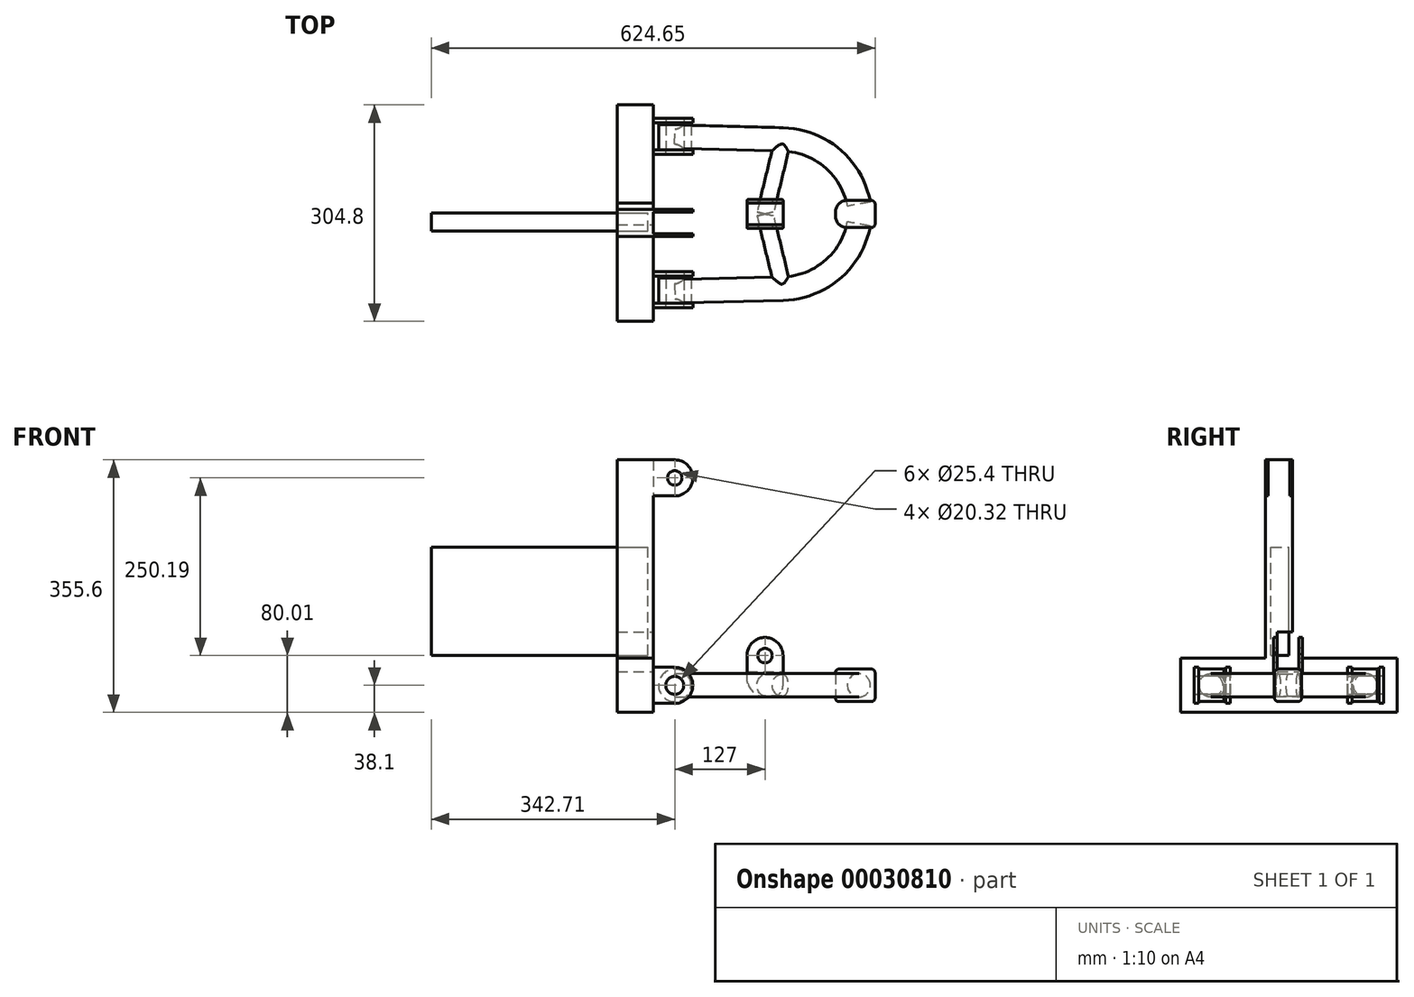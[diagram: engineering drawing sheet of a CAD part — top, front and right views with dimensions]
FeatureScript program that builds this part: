
annotation { "Feature Type Name" : "Feature", "Feature Type Description" : "" }
export const myFeature = defineFeature(function(context is Context, id is Id, definition is map)
    precondition{}
    {
        {
            var Q0;
            Q0=qCreatedBy(makeId("Front.planeOp"),FACE);
            var sketch = newSketch(context, id + "F0", { "sketchPlane" : qUnion([Q0])});
            skLineSegment(sketch, "E0.rect.bottom", {"start": v(-81.28, 38.1) * mm, "end": v(-30.48, 38.1) * mm});
            skLineSegment(sketch, "E0.rect.top", {"start": v(-81.28, -38.1) * mm, "end": v(-30.48, -38.1) * mm});
            skLineSegment(sketch, "E0.rect.left", {"start": v(-81.28, 38.1) * mm, "end": v(-81.28, -38.1) * mm});
            skLineSegment(sketch, "E0.rect.right", {"start": v(-30.48, 38.1) * mm, "end": v(-30.48, -38.1) * mm});
            skPoint(sketch, "E0.rect.middle", {"position": v(-55.88, 0) * mm});
            skCircle(sketch, "E1", {"center": v(0, 0) * mm, "radius": 12.7 * mm, "construction": true});
            skSolve(sketch);
        }
        {
            var Q0;
            Q0 = qSketchRegion(id + "F0", true);
            extrude(context, id + "F1", {"entities" : qUnion([Q0]), "endBound" : BoundingType.SYMMETRIC, "depth" : 304.8 * mm});
        }
        {
            var Q0;
            Q0=qCreatedBy(makeId("Front.planeOp"),FACE);
            cPlane(context, id + "F2", {"entities" : qUnion([Q0]), "cplaneType" : CPlaneType.OFFSET, "offset" : 127 * mm, "width" : 152.4 * mm, "height" : 152.4 * mm});
        }
        {
            var Q0;
            Q0=qCreatedBy(id+"F2.planeOp",FACE);
            cPlane(context, id + "F3", {"entities" : qUnion([Q0]), "cplaneType" : CPlaneType.OFFSET, "offset" : 38.1 * mm, "oppositeDirection" : true, "width" : 152.4 * mm, "height" : 152.4 * mm});
        }
        {
            var Q0;
            Q0=qCreatedBy(id+"F2.planeOp",FACE);
            var sketch = newSketch(context, id + "F4", { "sketchPlane" : qUnion([Q0])});
            skLineSegment(sketch, "E2.0", {"start": v(-30.48, 38.1) * mm, "end": v(-30.48, -38.1) * mm});
            skCircle(sketch, "E3", {"center": v(0, 0) * mm, "radius": 12.7 * mm});
            skLineSegment(sketch, "E4", {"start": v(-30.48, 25.4) * mm, "end": v(0, 25.4) * mm});
            skLineSegment(sketch, "E5", {"start": v(-30.48, -25.4) * mm, "end": v(0, -25.4) * mm});
            skArc(sketch, "E6", {"start": v(0, -25.4) * mm, "mid": v(25.4, 0) * mm, "end": v(0, 25.4) * mm});
            skLineSegment(sketch, "E7", {"start": v(0, 0) * mm, "end": v(-29.52, 0) * mm, "construction": true});
            skSolve(sketch);
        }
        {
            var Q0;
            Q0=qCreatedBy(id+"F3.planeOp",FACE);
            var sketch = newSketch(context, id + "F5", { "sketchPlane" : qUnion([Q0])});
            skLineSegment(sketch, "E8.0", {"start": v(-30.48, 25.4) * mm, "end": v(0, 25.4) * mm});
            skArc(sketch, "E8.1", {"start": v(0, -25.4) * mm, "mid": v(25.4, 0) * mm, "end": v(0, 25.4) * mm});
            skCircle(sketch, "E8.2", {"center": v(0, 0) * mm, "radius": 12.7 * mm});
            skLineSegment(sketch, "E8.3", {"start": v(-30.48, -25.4) * mm, "end": v(0, -25.4) * mm});
            skLineSegment(sketch, "E9.0", {"start": v(-30.48, 38.1) * mm, "end": v(-30.48, -38.1) * mm});
            skSolve(sketch);
        }
        {
            var Q0;
            Q0=makeQuery(id+"F4.imprint","IMPRINT",FACE,{"disambiguationData":[TD([[makeQuery(id+"F4.imprint","IMPRINT",EDGE,{"derivedFrom":sQuery(id+"F4.wireOp",EDGE,"E3")}),-1.0]])]});
            extrude(context, id + "F6", {"entities" : qUnion([Q0]), "depth" : 6.35 * mm});
        }
        {
            var Q0;
            {var subQ2=sQuery(id+"F5.wireOp",EDGE,"E8.0");Q0=makeQuery(id+"F5.imprint","IMPRINT",FACE,{"disambiguationData":[TD([[makeQuery(id+"F5.imprint","IMPRINT",EDGE,{"derivedFrom":subQ2}),-1.0]])]});}
            extrude(context, id + "F7", {"entities" : qUnion([Q0]), "oppositeDirection" : true, "depth" : 6.35 * mm});
        }
        {
            var Q0;
            Q0=makeQuery(id+"F7.opExtrude","SWEPT_BODY",BODY,{"disambiguationData":[OSD([sQuery(id+"F5.wireOp",EDGE,"E8.0"),sQuery(id+"F5.wireOp",EDGE,"E8.1"),sQuery(id+"F5.wireOp",EDGE,"E8.2"),sQuery(id+"F5.wireOp",EDGE,"E8.3"),sQuery(id+"F5.wireOp",EDGE,"E9.0")])]});
            var Q1;
            Q1=makeQuery(id+"F6.opExtrude","SWEPT_BODY",BODY,{"disambiguationData":[OSD([sQuery(id+"F4.wireOp",EDGE,"E2.0"),sQuery(id+"F4.wireOp",EDGE,"E3"),sQuery(id+"F4.wireOp",EDGE,"E4"),sQuery(id+"F4.wireOp",EDGE,"E5"),sQuery(id+"F4.wireOp",EDGE,"E6")])]});
            var Q2;
            Q2=qCreatedBy(makeId("Front.planeOp"),FACE);
            mirror(context, id + "F8", {"entities" : qUnion([Q0, Q1]), "mirrorPlane" : qUnion([Q2])});
        }
        {
            var Q0;
            Q0=makeQuery(id+"F8.opPattern","COPY",FACE,{"derivedFrom":makeQuery(id+"F7.opExtrude","CAP_FACE",FACE,{"disambiguationData":[OSD([sQuery(id+"F5.wireOp",EDGE,"E8.0"),sQuery(id+"F5.wireOp",EDGE,"E8.1"),sQuery(id+"F5.wireOp",EDGE,"E8.2"),sQuery(id+"F5.wireOp",EDGE,"E8.3"),sQuery(id+"F5.wireOp",EDGE,"E9.0")])],"isStart":true}),"instanceName":"1"});
            cPlane(context, id + "F9", {"entities" : qUnion([Q0]), "cplaneType" : CPlaneType.OFFSET, "offset" : 0 * mm, "width" : 152.4 * mm, "height" : 152.4 * mm});
        }
        {
            var Q0;
            Q0=qCreatedBy(id+"F2.planeOp",FACE);
            var sketch = newSketch(context, id + "F10", { "sketchPlane" : qUnion([Q0])});
            skCircle(sketch, "E10.0", {"center": v(0, 0) * mm, "radius": 12.7 * mm, "construction": true});
            skCircle(sketch, "E11", {"center": v(0, 0) * mm, "radius": 22.86 * mm});
            skSolve(sketch);
        }
        {
            var Q0;
            Q0 = qSketchRegion(id + "F10", true);
            extrude(context, id + "F11", {"entities" : qUnion([Q0]), "oppositeDirection" : true, "depth" : 35.56 * mm});
        }
        {
            var Q0;
            Q0=qCreatedBy(id+"F9.planeOp",FACE);
            var sketch = newSketch(context, id + "F12", { "sketchPlane" : qUnion([Q0])});
            skCircle(sketch, "E12.0", {"center": v(0, 0) * mm, "radius": 22.86 * mm});
            skSolve(sketch);
        }
        {
            var Q0;
            Q0=makeQuery(id+"F12.imprint","IMPRINT",FACE,{"disambiguationData":[TD([[makeQuery(id+"F12.imprint","IMPRINT",EDGE,{"derivedFrom":sQuery(id+"F12.wireOp",EDGE,"E12.0")}),1.0]])]});
            extrude(context, id + "F13", {"entities" : qUnion([Q0]), "depth" : 35.56 * mm});
        }
        {
            var Q0;
            Q0=makeQuery(id+"F1.opExtrude","SWEPT_FACE",FACE,{"disambiguationData":[OSD([sQuery(id+"F0.wireOp",EDGE,"E0.rect.bottom")])]});
            var sketch = newSketch(context, id + "F14", { "sketchPlane" : qUnion([Q0])});
            skLineSegment(sketch, "E13.0", {"start": v(-81.28, -152.4) * mm, "end": v(-81.28, 152.4) * mm});
            skLineSegment(sketch, "E13.1", {"start": v(-30.48, -152.4) * mm, "end": v(-30.48, 152.4) * mm});
            skLineSegment(sketch, "E14.bottom", {"start": v(-81.28, -33.02) * mm, "end": v(-30.48, -33.02) * mm});
            skLineSegment(sketch, "E14.top", {"start": v(-81.28, 5.08) * mm, "end": v(-30.48, 5.08) * mm});
            skLineSegment(sketch, "E14.left", {"start": v(-81.28, -33.02) * mm, "end": v(-81.28, 5.08) * mm});
            skLineSegment(sketch, "E14.right", {"start": v(-30.48, -33.02) * mm, "end": v(-30.48, 5.08) * mm});
            skSolve(sketch);
        }
        {
            var Q0;
            Q0 = qSketchRegion(id + "F14", true);
            extrude(context, id + "F15", {"entities" : qUnion([Q0]), "operationType" : NewBodyOperationType.ADD, "depth" : 279.4 * mm});
        }
        {
            var Q0;
            Q0=makeQuery(id+"F15.opExtrude","SWEPT_FACE",FACE,{"disambiguationData":[OSD([sQuery(id+"F14.wireOp",EDGE,"E14.bottom")])]});
            var sketch = newSketch(context, id + "F16", { "sketchPlane" : qUnion([Q0])});
            skPoint(sketch, "E15.0", {"position": v(-30.48, 317.5) * mm});
            skLineSegment(sketch, "E16.bottom", {"start": v(-30.48, 317.5) * mm, "end": v(0, 317.5) * mm});
            skLineSegment(sketch, "E16.top", {"start": v(-30.48, 266.7) * mm, "end": v(0, 266.7) * mm});
            skLineSegment(sketch, "E16.left", {"start": v(-30.48, 317.5) * mm, "end": v(-30.48, 266.7) * mm});
            skArc(sketch, "E17", {"start": v(0, 266.7) * mm, "mid": v(25.4, 292.1) * mm, "end": v(0, 317.5) * mm});
            skCircle(sketch, "E18", {"center": v(0, 292.1) * mm, "radius": 10.16 * mm});
            skSolve(sketch);
        }
        {
            var Q0;
            Q0=makeQuery(id+"F15.opExtrude","SWEPT_FACE",FACE,{"disambiguationData":[OSD([sQuery(id+"F14.wireOp",EDGE,"E14.top")])]});
            var sketch = newSketch(context, id + "F17", { "sketchPlane" : qUnion([Q0])});
            skLineSegment(sketch, "E19.0", {"start": v(30.48, 317.5) * mm, "end": v(30.48, 266.7) * mm});
            skLineSegment(sketch, "E19.1", {"start": v(30.48, 317.5) * mm, "end": v(0, 317.5) * mm});
            skLineSegment(sketch, "E19.2", {"start": v(30.48, 266.7) * mm, "end": v(0, 266.7) * mm});
            skArc(sketch, "E19.3", {"start": v(0, 266.7) * mm, "mid": v(-25.4, 292.1) * mm, "end": v(0, 317.5) * mm});
            skCircle(sketch, "E19.4", {"center": v(0, 292.1) * mm, "radius": 10.16 * mm});
            skSolve(sketch);
        }
        {
            var Q0;
            Q0=makeQuery(id+"F16.imprint","IMPRINT",FACE,{"disambiguationData":[TD([[makeQuery(id+"F16.imprint","IMPRINT",EDGE,{"derivedFrom":sQuery(id+"F16.wireOp",EDGE,"E16.bottom")}),-1.0]])]});
            extrude(context, id + "F18", {"entities" : qUnion([Q0]), "operationType" : NewBodyOperationType.ADD, "oppositeDirection" : true, "depth" : 3.8 * mm});
        }
        {
            var Q0;
            Q0=makeQuery(id+"F17.imprint","IMPRINT",FACE,{"disambiguationData":[TD([[makeQuery(id+"F17.imprint","IMPRINT",EDGE,{"derivedFrom":sQuery(id+"F17.wireOp",EDGE,"E19.0")}),-1.0]])]});
            extrude(context, id + "F19", {"entities" : qUnion([Q0]), "operationType" : NewBodyOperationType.ADD, "oppositeDirection" : true, "depth" : 3.8 * mm});
        }
        {
            var Q0;
            Q0=qCreatedBy(makeId("Top.planeOp"),FACE);
            var sketch = newSketch(context, id + "F20", { "sketchPlane" : qUnion([Q0])});
            skLineSegment(sketch, "E20.0", {"start": v(-22.86, 124.46) * mm, "end": v(22.86, 124.46) * mm});
            skPoint(sketch, "E20.1", {"position": v(0, 88.9) * mm});
            skLineSegment(sketch, "E20.2", {"start": v(22.86, -91.44) * mm, "end": v(-22.86, -91.44) * mm});
            skPoint(sketch, "E20.3", {"position": v(0, -127) * mm});
            skLineSegment(sketch, "E21", {"start": v(0, -91.44) * mm, "end": v(0, -127) * mm, "construction": true});
            skLineSegment(sketch, "E22", {"start": v(0, 88.9) * mm, "end": v(0, 124.46) * mm, "construction": true});
            skLineSegment(sketch, "E23.rect.bottom", {"start": v(281.94, 17.78) * mm, "end": v(226.06, 17.78) * mm});
            skLineSegment(sketch, "E23.rect.top", {"start": v(281.94, -20.32) * mm, "end": v(226.06, -20.32) * mm});
            skLineSegment(sketch, "E23.rect.left", {"start": v(281.94, 17.78) * mm, "end": v(281.94, -20.32) * mm});
            skLineSegment(sketch, "E23.rect.right", {"start": v(226.06, 17.78) * mm, "end": v(226.06, -20.32) * mm});
            skPoint(sketch, "E23.rect.middle", {"position": v(254, -1.27) * mm});
            skLineSegment(sketch, "E24.0", {"start": v(22.86, -85.1) * mm, "end": v(-22.86, -85.1) * mm});
            skLineSegment(sketch, "E25", {"start": v(0, 107.7) * mm, "end": v(152.4, 103.7) * mm});
            skLineSegment(sketch, "E26.0", {"start": v(22.86, -127) * mm, "end": v(-22.86, -127) * mm});
            skLineSegment(sketch, "E27", {"start": v(22.86, 124.46) * mm, "end": v(22.86, -127) * mm, "construction": true});
            skPoint(sketch, "E28", {"position": v(22.86, -1.27) * mm});
            skLineSegment(sketch, "E29", {"start": v(22.86, -1.27) * mm, "end": v(68.58, -1.27) * mm, "construction": true});
            skArc(sketch, "E30", {"start": v(152.4, 103.7) * mm, "mid": v(221.84, 77.07) * mm, "end": v(259.08, 12.7) * mm});
            skLineSegment(sketch, "E31.rect.bottom", {"start": v(151.13, 19.05) * mm, "end": v(102.87, 19.05) * mm});
            skLineSegment(sketch, "E31.rect.top", {"start": v(151.13, -21.59) * mm, "end": v(102.87, -21.59) * mm});
            skLineSegment(sketch, "E31.rect.left", {"start": v(152.4, 17.78) * mm, "end": v(152.4, -20.32) * mm});
            skLineSegment(sketch, "E31.rect.right", {"start": v(101.6, 17.78) * mm, "end": v(101.6, -20.32) * mm});
            skPoint(sketch, "E31.rect.middle", {"position": v(127, -1.27) * mm});
            skLineSegment(sketch, "E32", {"start": v(127, -1.27) * mm, "end": v(152.4, 103.7) * mm});
            skPoint(sketch, "E33.visualSharp", {"position": v(101.6, 19.05) * mm});
            skArc(sketch, "E33.filletArc", {"start": v(102.87, 19.05) * mm, "mid": v(101.97, 18.68) * mm, "end": v(101.6, 17.78) * mm});
            skPoint(sketch, "E34.visualSharp", {"position": v(152.4, 19.05) * mm});
            skArc(sketch, "E34.filletArc", {"start": v(152.4, 17.78) * mm, "mid": v(152.03, 18.68) * mm, "end": v(151.13, 19.05) * mm});
            skPoint(sketch, "E35.visualSharp", {"position": v(152.4, -21.59) * mm});
            skArc(sketch, "E35.filletArc", {"start": v(151.13, -21.59) * mm, "mid": v(152.03, -21.22) * mm, "end": v(152.4, -20.32) * mm});
            skPoint(sketch, "E36.visualSharp", {"position": v(101.6, -21.59) * mm});
            skArc(sketch, "E36.filletArc", {"start": v(101.6, -20.32) * mm, "mid": v(101.97, -21.22) * mm, "end": v(102.87, -21.59) * mm});
            skSolve(sketch);
        }
        {
            var Q0;
            Q0=makeQuery(id+"F20.imprint","IMPRINT",FACE,{"disambiguationData":[TD([[makeQuery(id+"F20.imprint","IMPRINT",EDGE,{"derivedFrom":sQuery(id+"F20.wireOp",EDGE,"E23.rect.bottom")}),-1.0]])]});
            var Q1;
            Q1=makeQuery(id+"F20.imprint","IMPRINT",FACE,{"disambiguationData":[TD([[makeQuery(id+"F20.imprint","IMPRINT",EDGE,{"derivedFrom":sQuery(id+"F20.wireOp",EDGE,"E23.rect.bottom")}),1.0]])]});
            extrude(context, id + "F21", {"entities" : qUnion([Q0, Q1]), "endBound" : BoundingType.SYMMETRIC, "depth" : 45.72 * mm});
        }
        {
            var Q0;
            Q0=sQuery(id+"F20.wireOp",EDGE,"E25");
            var Q1;
            Q1=sQuery(id+"F20.wireOp",VERTEX,"E25.start");
            cPlane(context, id + "F22", {"entities" : qUnion([Q0, Q1]), "cplaneType" : CPlaneType.LINE_POINT, "offset" : 152.4 * mm, "width" : 152.4 * mm, "height" : 152.4 * mm});
        }
        {
            var Q0;
            Q0=qCreatedBy(id+"F22.planeOp",FACE);
            var sketch = newSketch(context, id + "F23", { "sketchPlane" : qUnion([Q0])});
            skCircle(sketch, "E37", {"center": v(107.66, 0) * mm, "radius": 16.51 * mm});
            skSolve(sketch);
        }
        {
            var Q0;
            Q0=makeQuery(id+"F23.imprint","IMPRINT",FACE,{"disambiguationData":[TD([[makeQuery(id+"F23.imprint","IMPRINT",EDGE,{"derivedFrom":sQuery(id+"F23.wireOp",EDGE,"E37")}),1.0]])]});
            var Q1;
            Q1=sQuery(id+"F20.wireOp",EDGE,"E25");
            var Q2;
            Q2=sQuery(id+"F20.wireOp",EDGE,"E30");
            sweep(context, id + "F24", {"profiles" : qUnion([Q0]), "path" : qUnion([Q1, Q2])});
        }
        {
            var Q0;
            Q0=sQuery(id+"F20.wireOp",EDGE,"E32");
            var Q1;
            Q1=sQuery(id+"F20.wireOp",VERTEX,"E31.rect.middle");
            cPlane(context, id + "F25", {"entities" : qUnion([Q0, Q1]), "cplaneType" : CPlaneType.LINE_POINT, "offset" : 152.4 * mm, "width" : 152.4 * mm, "height" : 152.4 * mm});
        }
        {
            var Q0;
            Q0=qCreatedBy(id+"F25.planeOp",FACE);
            var sketch = newSketch(context, id + "F26", { "sketchPlane" : qUnion([Q0])});
            skEllipse(sketch, "E38", {"center": v(-123.74, 0) * mm, "majorRadius": 11.43 * mm, "minorRadius": 15.24 * mm, "majorAxis": v(-1, 0)});
            skLineSegment(sketch, "E39", {"start": v(-123.74, 0) * mm, "end": v(-139.12, 0) * mm, "construction": true});
            skLineSegment(sketch, "E40", {"start": v(-123.74, 15.24) * mm, "end": v(-123.74, 0) * mm, "construction": true});
            skSolve(sketch);
        }
        {
            var Q0;
            Q0=makeQuery(id+"F26.imprint","IMPRINT",FACE,{"disambiguationData":[TD([[makeQuery(id+"F26.imprint","IMPRINT",EDGE,{"derivedFrom":sQuery(id+"F26.wireOp",EDGE,"E38")}),1.0]])]});
            var Q1;
            Q1=sQuery(id+"F20.wireOp",EDGE,"E32");
            sweep(context, id + "F27", {"operationType" : NewBodyOperationType.ADD, "profiles" : qUnion([Q0]), "path" : qUnion([Q1])});
        }
        {
            var Q0;
            Q0=makeQuery(id+"F20.imprint","IMPRINT",FACE,{"disambiguationData":[TD([[makeQuery(id+"F20.imprint","IMPRINT",EDGE,{"derivedFrom":sQuery(id+"F20.wireOp",EDGE,"E31.rect.top")}),-1.0]])]});
            extrude(context, id + "F28", {"entities" : qUnion([Q0]), "oppositeDirection" : true, "depth" : 16.5 * mm, "hasSecondDirection" : true, "secondDirectionOppositeDirection" : false, "secondDirectionDepth" : 67.3 * mm});
        }
        {
            var Q0;
            Q0=sQuery(id+"F20.wireOp",EDGE,"E27");
            var Q1;
            Q1=sQuery(id+"F20.wireOp",VERTEX,"E28");
            cPlane(context, id + "F29", {"entities" : qUnion([Q0, Q1]), "cplaneType" : CPlaneType.LINE_POINT, "offset" : 152.4 * mm, "width" : 152.4 * mm, "height" : 152.4 * mm});
        }
        {
            var Q0;
            Q0=makeQuery(id+"F28.opExtrude","SWEPT_FACE",FACE,{"disambiguationData":[OSD([sQuery(id+"F20.wireOp",EDGE,"E31.rect.top")])]});
            var sketch = newSketch(context, id + "F30", { "sketchPlane" : qUnion([Q0])});
            skLineSegment(sketch, "E41.0", {"start": v(152.4, -16.5) * mm, "end": v(152.4, 67.31) * mm, "construction": true});
            skLineSegment(sketch, "E41.1", {"start": v(101.6, -16.5) * mm, "end": v(101.6, 67.31) * mm, "construction": true});
            skArc(sketch, "E42", {"start": v(152.4, 41.91) * mm, "mid": v(127, 67.31) * mm, "end": v(101.6, 41.91) * mm});
            skLineSegment(sketch, "E43", {"start": v(152.4, 41.91) * mm, "end": v(160.28, 41.91) * mm});
            skLineSegment(sketch, "E44", {"start": v(160.28, 41.91) * mm, "end": v(160.28, 73.44) * mm});
            skLineSegment(sketch, "E45", {"start": v(160.28, 73.44) * mm, "end": v(127, 73.44) * mm});
            skLineSegment(sketch, "E46", {"start": v(127, 73.44) * mm, "end": v(127, 41.91) * mm, "construction": true});
            skLineSegment(sketch, "E47.MirrorCS", {"start": v(93.72, 73.44) * mm, "end": v(127, 73.44) * mm});
            skLineSegment(sketch, "E48.MirrorCS", {"start": v(93.72, 41.91) * mm, "end": v(93.72, 73.44) * mm});
            skLineSegment(sketch, "E49.MirrorCS", {"start": v(101.6, 41.91) * mm, "end": v(93.72, 41.91) * mm});
            skCircle(sketch, "E50", {"center": v(127, 41.91) * mm, "radius": 10.16 * mm});
            skSolve(sketch);
        }
        {
            var Q0;
            Q0 = qSketchRegion(id + "F30", true);
            extrude(context, id + "F31", {"entities" : qUnion([Q0]), "operationType" : NewBodyOperationType.REMOVE, "endBound" : BoundingType.THROUGH_ALL, "oppositeDirection" : true, "depth" : 25.4 * mm});
        }
        {
            var Q0;
            Q0=makeQuery(id+"F28.opExtrude","SWEPT_FACE",FACE,{"disambiguationData":[OSD([sQuery(id+"F20.wireOp",EDGE,"E31.rect.left")])]});
            var sketch = newSketch(context, id + "F32", { "sketchPlane" : qUnion([Q0])});
            skLineSegment(sketch, "E51.0", {"start": v(-21.6, 49.84) * mm, "end": v(-21.6, 67.31) * mm});
            skLineSegment(sketch, "E52.0", {"start": v(19.05, 67.31) * mm, "end": v(19.05, 49.84) * mm});
            skLineSegment(sketch, "E53", {"start": v(-21.6, 49.84) * mm, "end": v(19.05, 49.84) * mm, "construction": true});
            skLineSegment(sketch, "E54", {"start": v(-1.27, 49.84) * mm, "end": v(-1.27, 47) * mm, "construction": true});
            skLineSegment(sketch, "E55.rect.bottom", {"start": v(13.97, 74.93) * mm, "end": v(-16.51, 74.93) * mm});
            skLineSegment(sketch, "E55.rect.top", {"start": v(13.97, 19.05) * mm, "end": v(-16.51, 19.05) * mm});
            skLineSegment(sketch, "E55.rect.left", {"start": v(13.97, 74.93) * mm, "end": v(13.97, 19.05) * mm});
            skLineSegment(sketch, "E55.rect.right", {"start": v(-16.51, 74.93) * mm, "end": v(-16.51, 19.05) * mm});
            skPoint(sketch, "E55.rect.middle", {"position": v(-1.27, 47) * mm});
            skPoint(sketch, "E56.1", {"position": v(-1.27, 0) * mm});
            skSolve(sketch);
        }
        {
            var Q0;
            Q0 = qSketchRegion(id + "F32", true);
            extrude(context, id + "F33", {"entities" : qUnion([Q0]), "operationType" : NewBodyOperationType.REMOVE, "endBound" : BoundingType.THROUGH_ALL, "oppositeDirection" : true, "depth" : 25.4 * mm});
        }
        {
            var Q0;
            Q0=makeQuery(id+"F24.opSweep","SWEPT_BODY",BODY,{"disambiguationData":[OSD([sQuery(id+"F20.wireOp",EDGE,"47162161-0d8e-436a-9f51-dbf66ce8a4d5"),sQuery(id+"F23.wireOp",EDGE,"E37")])]});
            var Q1;
            Q1=qCreatedBy(id+"F29.planeOp",FACE);
            mirror(context, id + "F34", {"entities" : qUnion([Q0]), "mirrorPlane" : qUnion([Q1])});
        }
        {
            var Q0;
            Q0=makeQuery(id+"F4.imprint","IMPRINT",FACE,{"disambiguationData":[TD([[makeQuery(id+"F4.imprint","IMPRINT",EDGE,{"derivedFrom":sQuery(id+"F4.wireOp",EDGE,"E3")}),1.0]])]});
            extrude(context, id + "F35", {"entities" : qUnion([Q0]), "operationType" : NewBodyOperationType.REMOVE, "endBound" : BoundingType.THROUGH_ALL, "oppositeDirection" : true, "depth" : 25.4 * mm});
        }
        {
            var Q0;
            Q0=makeQuery(id+"F28.opExtrude","CAP_EDGE",EDGE,{"disambiguationData":[OSD([sQuery(id+"F20.wireOp",EDGE,"E31.rect.right")])],"isStart":false});
            fillet(context, id + "F36", {"entities" : qUnion([Q0]), "radius" : 27.32 * mm, "allowEdgeOverflow" : false});
        }
        {
            var Q0;
            Q0=makeQuery(id+"F28.opExtrude","CAP_EDGE",EDGE,{"disambiguationData":[OSD([sQuery(id+"F20.wireOp",EDGE,"E31.rect.left")])],"isStart":false});
            var Q1;
            Q1=makeQuery(id+"F21.opExtrude","SWEPT_EDGE",EDGE,{"disambiguationData":[OSD([sQuery(id+"F20.wireOp",EDGE,"E23.rect.top"),sQuery(id+"F20.wireOp",EDGE,"E23.rect.right")])]});
            var Q2;
            Q2=makeQuery(id+"F21.opExtrude","SWEPT_EDGE",EDGE,{"disambiguationData":[OSD([sQuery(id+"F20.wireOp",EDGE,"E23.rect.bottom"),sQuery(id+"F20.wireOp",EDGE,"E23.rect.right")])]});
            fillet(context, id + "F37", {"entities" : qUnion([Q0, Q1, Q2]), "radius" : 16.51 * mm, "allowEdgeOverflow" : false});
        }
        {
            var Q0;
            Q0=makeQuery(id+"F21.opExtrude","SWEPT_EDGE",EDGE,{"disambiguationData":[OSD([sQuery(id+"F20.wireOp",EDGE,"E23.rect.top"),sQuery(id+"F20.wireOp",EDGE,"E23.rect.left")])]});
            var Q1;
            Q1=makeQuery(id+"F21.opExtrude","SWEPT_EDGE",EDGE,{"disambiguationData":[OSD([sQuery(id+"F20.wireOp",EDGE,"E23.rect.bottom"),sQuery(id+"F20.wireOp",EDGE,"E23.rect.left")])]});
            var Q2;
            Q2=makeQuery(id+"F21.opExtrude","CAP_EDGE",EDGE,{"disambiguationData":[OSD([sQuery(id+"F20.wireOp",EDGE,"E23.rect.top")])],"isStart":false});
            var Q3;
            Q3=makeQuery(id+"F21.opExtrude","CAP_EDGE",EDGE,{"disambiguationData":[OSD([sQuery(id+"F20.wireOp",EDGE,"E23.rect.left")])],"isStart":false});
            var Q4;
            Q4=makeQuery(id+"F21.opExtrude","CAP_EDGE",EDGE,{"disambiguationData":[OSD([sQuery(id+"F20.wireOp",EDGE,"E23.rect.top")])],"isStart":true});
            var Q5;
            Q5=makeQuery(id+"F21.opExtrude","CAP_EDGE",EDGE,{"disambiguationData":[OSD([sQuery(id+"F20.wireOp",EDGE,"E23.rect.left")])],"isStart":true});
            fillet(context, id + "F38", {"entities" : qUnion([Q0, Q1, Q2, Q3, Q4, Q5]), "radius" : 5.08 * mm, "tangentPropagation" : true, "allowEdgeOverflow" : false});
        }
        {
            var Q0;
            Q0=qCreatedBy(makeId("Front.planeOp"),FACE);
            var sketch = newSketch(context, id + "F39", { "sketchPlane" : qUnion([Q0])});
            skLineSegment(sketch, "E57.bottom", {"start": v(-342.7, 42.18) * mm, "end": v(-37.9, 42.18) * mm});
            skLineSegment(sketch, "E57.top", {"start": v(-342.7, 194.58) * mm, "end": v(-37.9, 194.58) * mm});
            skLineSegment(sketch, "E57.left", {"start": v(-342.7, 42.18) * mm, "end": v(-342.7, 194.58) * mm});
            skLineSegment(sketch, "E57.right", {"start": v(-37.9, 42.18) * mm, "end": v(-37.9, 194.58) * mm});
            skSolve(sketch);
        }
        {
            var Q0;
            Q0=makeQuery(id+"F39.imprint","IMPRINT",FACE,{"disambiguationData":[TD([[makeQuery(id+"F39.imprint","IMPRINT",EDGE,{"derivedFrom":sQuery(id+"F39.wireOp",EDGE,"E57.bottom")}),1.0]])]});
            extrude(context, id + "F40", {"entities" : qUnion([Q0]), "depth" : 25.4 * mm});
        }
    });
